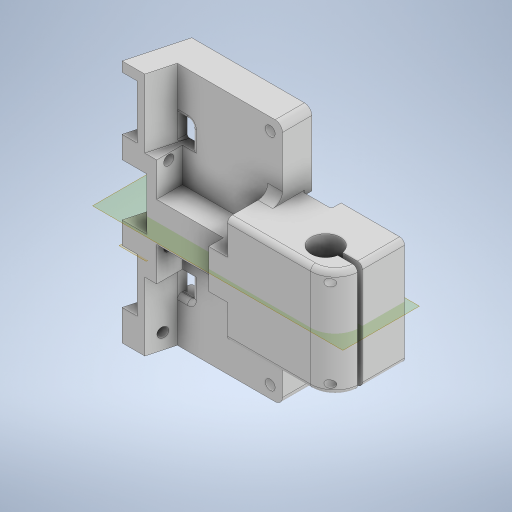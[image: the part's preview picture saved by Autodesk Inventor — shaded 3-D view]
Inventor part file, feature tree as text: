
AUTODESK INVENTOR PART (.ipt)
format: ipt  version: 2023 (Build 270158000, 158)  size: 1,031,680 bytes
history: native  units: in
note: dims shown in document units (in); Inventor stores cm internally (conversion verified against a paired STEP export)
features: projected_geometry x38, sketch x33, extrude x29, reference x26, fillet x15, other x11, hole x4, chamfer x1, mirror x1
ambient origin geometry x8: Origin, YZ Plane, XZ Plane, XY Plane, X Axis, Y Axis, Z Axis, Center Point
bodies: Body1 (feature_tree)
feature tree (158):
  other  "Bryła1"
  sketch  "Szkic1"
  other  "Płaszczyzna konstrukcyjna1"
  extrude  "Wyciągnięcie proste1"  Depth=1.9685in
  extrude  "Wyciągnięcie proste2"  Depth=1.9685in
  extrude  "Wyciągnięcie proste3"  Depth=0.8661in
  extrude  "Wyciągnięcie proste4"  Depth=0.0394in
  extrude  "Wyciągnięcie proste5"  Depth=0.0394in
  extrude  "Wyciągnięcie proste6"  Depth=0.3937in TaperAngle=0.0deg
  extrude  "Wyciągnięcie proste7"  Depth=1.9685in
  extrude  "Wyciągnięcie proste8"  Depth=0.9843in
  extrude  "Wyciągnięcie proste9"  Depth=1.9685in
  extrude  "Wyciągnięcie proste10"  Depth=0.9843in
  hole  "Otwór1"  [1 undecoded]
  hole  "Otwór2"  [1 undecoded]
  other  "Płaszczyzna konstrukcyjna2"
  extrude  "Wyciągnięcie proste12"  TaperAngle=0.0deg  [1 undecoded]
  fillet  "Zaokrąglenie1"  Radius=0.0787in
  extrude  "Wyciągnięcie proste13"  TaperAngle=0.0deg  [1 undecoded]
  extrude  "Wyciągnięcie proste14"  Depth=0.248in
  extrude  "Wyciągnięcie proste15"  Depth=0.0787in
  extrude  "Wyciągnięcie proste16"  Depth=0.2165in
  extrude  "Wyciągnięcie proste17"  Depth=0.2165in
  extrude  "Wyciągnięcie proste20"  Depth=0.4331in
  extrude  "Wyciągnięcie proste21"  Depth=0.4331in
  chamfer  "Faza1"  Distance=0.5906in
  fillet  "Zaokrąglenie7"  Radius=0.1181in
  extrude  "Wyciągnięcie proste22"  Depth=0.1181in TaperAngle=0.0deg
  extrude  "Wyciągnięcie proste23"  Depth=0.0787in TaperAngle=0.0deg
  extrude  "Wyciągnięcie proste24"  Depth=0.0197in
  extrude  "Wyciągnięcie proste25"  Depth=0.0197in
  fillet  "Zaokrąglenie11"  [1 undecoded]
  hole  "Otwór5"  [1 undecoded]
  fillet  "Zaokrąglenie13"  Radius=0.7756in
  fillet  "Zaokrąglenie14"  Radius=0.1969in
  extrude  "Wyciągnięcie proste26"  Depth=0.1772in
  fillet  "Zaokrąglenie18"  Radius=0.1772in
  extrude  "Wyciągnięcie proste27"  Depth=0.7756in TaperAngle=0.0deg
  fillet  "Zaokrąglenie20"  Radius=0.1575in
  fillet  "Zaokrąglenie22"  Radius=0.1575in
  fillet  "Zaokrąglenie23"  Radius=0.1575in
  extrude  "Wyciągnięcie proste28"  Depth=0.1575in TaperAngle=0.0deg
  extrude  "Wyciągnięcie proste29"  Depth=0.0787in
  extrude  "Wyciągnięcie proste30"  TaperAngle=0.0deg  [1 undecoded]
  fillet  "Zaokrąglenie24"  Radius=0.3937in
  fillet  "Zaokrąglenie25"  Radius=0.3937in
  other  "Płaszczyzna konstrukcyjna3"
  mirror  "Odbij1"
  extrude  "Wyciągnięcie proste31"  Depth=0.1583in
  fillet  "Zaokrąglenie26"  Radius=0.0354in
  extrude  "Wyciągnięcie proste32"  Depth=0.0354in
  hole  "Otwór6"  [1 undecoded]
  fillet  "Zaokrąglenie27"  Radius=0.0394in
  fillet  "Zaokrąglenie28"  Radius=0.0394in
  fillet  "Zaokrąglenie29"  Radius=0.0394in
  reference  "Odniesienie1"
  reference  "Odniesienie2"
  reference  "Odniesienie3"
  reference  "Odniesienie4"
  reference  "Odniesienie5"
  reference  "Odniesienie6"
  reference  "Odniesienie7"
  reference  "Odniesienie8"
  reference  "Odniesienie9"
  reference  "Odniesienie10"
  reference  "Odniesienie11"
  reference  "Odniesienie12"
  reference  "Odniesienie13"
  sketch  "Szkic2"
  reference  "Odniesienie14"
  reference  "Odniesienie15"
  reference  "Odniesienie16"
  reference  "Odniesienie17"
  reference  "Odniesienie18"
  reference  "Odniesienie19"
  reference  "Odniesienie20"
  reference  "Odniesienie21"
  reference  "Odniesienie22"
  reference  "Odniesienie23"
  sketch  "Szkic3"
  reference  "Odniesienie24"
  projected_geometry  "Pętla rzutowana1"
  sketch  "Szkic4"
  reference  "Odniesienie25"
  sketch  "Szkic5"
  projected_geometry  "Pętla rzutowana2"
  projected_geometry  "Pętla rzutowana3"
  sketch  "Szkic6"
  reference  "Odniesienie26"
  projected_geometry  "Pętla rzutowana4"
  sketch  "Szkic7"
  projected_geometry  "Pętla rzutowana5"
  sketch  "Szkic8"
  projected_geometry  "Pętla rzutowana6"
  projected_geometry  "Pętla rzutowana7"
  sketch  "Szkic9"
  projected_geometry  "Pętla rzutowana8"
  sketch  "Szkic10"
  sketch  "Szkic11"
  projected_geometry  "Pętla rzutowana9"
  sketch  "Szkic12"
  sketch  "Szkic14"
  projected_geometry  "Pętla rzutowana11"
  sketch  "Szkic15"
  projected_geometry  "Pętla rzutowana12"
  sketch  "Szkic16"
  projected_geometry  "Pętla rzutowana13"
  sketch  "Szkic18"
  projected_geometry  "Pętla rzutowana16"
  sketch  "Szkic19"
  projected_geometry  "Pętla rzutowana17"
  sketch  "Szkic20"
  projected_geometry  "Pętla rzutowana18"
  projected_geometry  "Pętla rzutowana19"
  sketch  "Szkic23"
  projected_geometry  "Pętla rzutowana21"
  sketch  "Szkic24"
  projected_geometry  "Pętla rzutowana22"
  sketch  "Szkic25"
  projected_geometry  "Pętla rzutowana23"
  projected_geometry  "Pętla rzutowana24"
  sketch  "Szkic26"
  projected_geometry  "Pętla rzutowana25"
  projected_geometry  "Pętla rzutowana26"
  sketch  "Szkic27"
  projected_geometry  "Pętla rzutowana27"
  sketch  "Szkic28"
  projected_geometry  "Pętla rzutowana28"
  sketch  "Szkic30"
  projected_geometry  "Pętla rzutowana31"
  projected_geometry  "Pętla rzutowana32"
  sketch  "Szkic31"
  projected_geometry  "Pętla rzutowana33"
  projected_geometry  "Pętla rzutowana34"
  sketch  "Szkic32"
  projected_geometry  "Pętla rzutowana35"
  sketch  "Szkic33"
  projected_geometry  "Pętla rzutowana36"
  sketch  "Szkic34"
  projected_geometry  "Pętla rzutowana37"
  sketch  "Szkic35"
  projected_geometry  "Pętla rzutowana38"
  sketch  "Szkic36"
  projected_geometry  "Pętla rzutowana39"
  projected_geometry  "Pętla rzutowana40"
  sketch  "Szkic37"
  projected_geometry  "Pętla rzutowana41"
  sketch  "Szkic38"
  projected_geometry  "Pętla rzutowana42"
  projected_geometry  "Pętla rzutowana43"
  projected_geometry  "Pętla rzutowana44"
  other  "<userpath>\Documents\PROJECTS - repos\Stratos---MicroSumo\mechanics\byk_alternator.iam"
  other  "byk_alternator.iam"
  other  "servo_mini_1370hd_cos:1"
  other  "servo_mini_1370hd_cos:2"
  other  "Zespół1"
  other  "uchwyt silnikow:1"
  other  "noz2:1"
note: 8 required parameter values undecoded (feature->parameter linkage not recoverable at this tier; creation-order binding heuristic only, values carry confidence <= 0.55)
